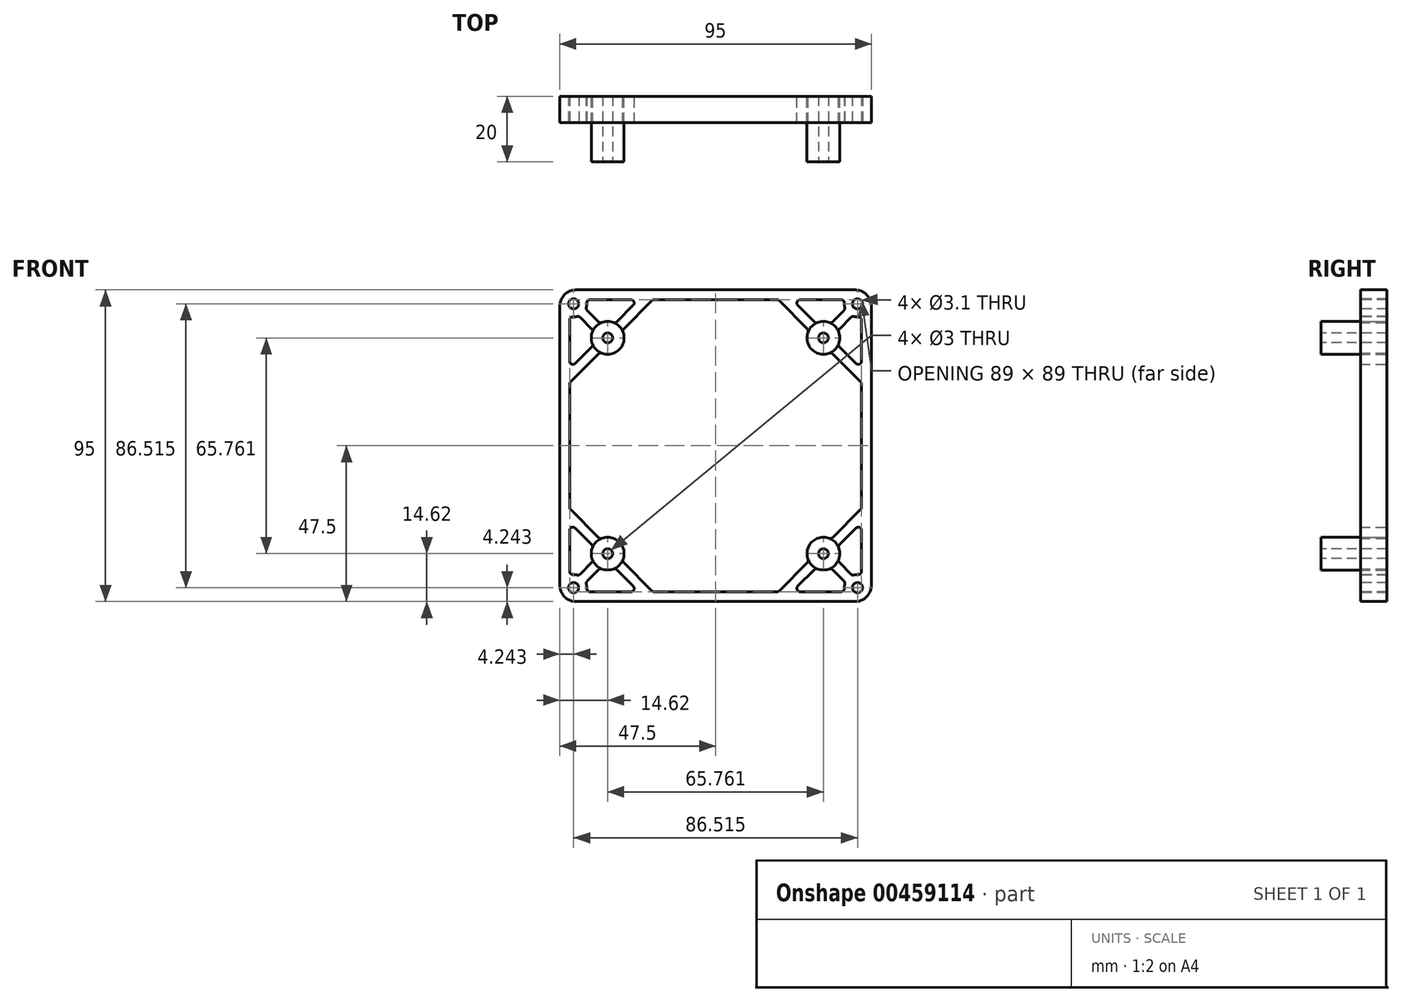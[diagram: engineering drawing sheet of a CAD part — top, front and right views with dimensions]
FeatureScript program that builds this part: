
annotation { "Feature Type Name" : "Feature", "Feature Type Description" : "" }
export const myFeature = defineFeature(function(context is Context, id is Id, definition is map)
    precondition{}
    {
        {
            var Q0;
            Q0=qCreatedBy(makeId("Front.planeOp"),FACE);
            var sketch = newSketch(context, id + "F0", { "sketchPlane" : qUnion([Q0])});
            skCircle(sketch, "E0", {"center": v(0, 0) * mm, "radius": 46.5 * mm, "construction": true});
            skLineSegment(sketch, "E1.bottom", {"start": v(-47.5, 47.5) * mm, "end": v(47.5, 47.5) * mm});
            skLineSegment(sketch, "E1.top", {"start": v(-47.5, -47.5) * mm, "end": v(47.5, -47.5) * mm});
            skLineSegment(sketch, "E1.left", {"start": v(-47.5, 47.5) * mm, "end": v(-47.5, -47.5) * mm});
            skLineSegment(sketch, "E1.right", {"start": v(47.5, 47.5) * mm, "end": v(47.5, -47.5) * mm});
            skLineSegment(sketch, "E2", {"start": v(-47.5, 47.5) * mm, "end": v(0, 0) * mm, "construction": true});
            skLineSegment(sketch, "E3", {"start": v(0, 0) * mm, "end": v(-47.5, 0) * mm, "construction": true});
            skSolve(sketch);
        }
        {
            var Q0;
            Q0=qSketchRegion(id+"F0",true);
            extrude(context, id + "F1", {"entities" : qUnion([Q0]), "depth" : 8 * mm});
        }
        {
            var Q0;
            Q0=makeQuery(id+"F1.opExtrude","CAP_FACE",FACE,{"disambiguationData":[OSD([sQuery(id+"F0.wireOp",EDGE,"E1.bottom"),sQuery(id+"F0.wireOp",EDGE,"E1.top"),sQuery(id+"F0.wireOp",EDGE,"E1.left"),sQuery(id+"F0.wireOp",EDGE,"E1.right"),sQuery(id+"F0.wireOp",EDGE,"Br8Wk0Kl-JEZb-qdU3-erjV-k9UwIw1fq8sk"),sQuery(id+"F0.wireOp",EDGE,"a4S6U98I-Ht7V-EsoT-nMCl-3wyK6It4gxP9"),sQuery(id+"F0.wireOp",EDGE,"JVSH8V9o-5ynY-7XZ7-INyu-qKdjU10l5uuq"),sQuery(id+"F0.wireOp",EDGE,"e923e9d5-6f60-4271-b24b-f0056a6a55640.MirrorCS"),sQuery(id+"F0.wireOp",EDGE,"e923e9d5-6f60-4271-b24b-f0056a6a55641.MirrorCS"),sQuery(id+"F0.wireOp",EDGE,"6366cbee-bac9-4992-bea0-77eb415f6a07.1.0"),sQuery(id+"F0.wireOp",EDGE,"6366cbee-bac9-4992-bea0-77eb415f6a07.1.1"),sQuery(id+"F0.wireOp",EDGE,"6366cbee-bac9-4992-bea0-77eb415f6a07.1.2"),sQuery(id+"F0.wireOp",EDGE,"6366cbee-bac9-4992-bea0-77eb415f6a07.1.3"),sQuery(id+"F0.wireOp",EDGE,"6366cbee-bac9-4992-bea0-77eb415f6a07.1.4"),sQuery(id+"F0.wireOp",EDGE,"6366cbee-bac9-4992-bea0-77eb415f6a07.2.0"),sQuery(id+"F0.wireOp",EDGE,"6366cbee-bac9-4992-bea0-77eb415f6a07.2.1"),sQuery(id+"F0.wireOp",EDGE,"6366cbee-bac9-4992-bea0-77eb415f6a07.2.2"),sQuery(id+"F0.wireOp",EDGE,"6366cbee-bac9-4992-bea0-77eb415f6a07.2.3"),sQuery(id+"F0.wireOp",EDGE,"6366cbee-bac9-4992-bea0-77eb415f6a07.2.4"),sQuery(id+"F0.wireOp",EDGE,"6366cbee-bac9-4992-bea0-77eb415f6a07.3.0"),sQuery(id+"F0.wireOp",EDGE,"6366cbee-bac9-4992-bea0-77eb415f6a07.3.1"),sQuery(id+"F0.wireOp",EDGE,"6366cbee-bac9-4992-bea0-77eb415f6a07.3.2"),sQuery(id+"F0.wireOp",EDGE,"6366cbee-bac9-4992-bea0-77eb415f6a07.3.3"),sQuery(id+"F0.wireOp",EDGE,"6366cbee-bac9-4992-bea0-77eb415f6a07.3.4")])],"isStart":false});
            var sketch = newSketch(context, id + "F2", { "sketchPlane" : qUnion([Q0])});
            skCircle(sketch, "E4", {"center": v(-43.26, 43.26) * mm, "radius": 1.55 * mm});
            skLineSegment(sketch, "E5", {"start": v(-34.04, 47.5) * mm, "end": v(-47.5, 47.5) * mm, "construction": true});
            skLineSegment(sketch, "E6", {"start": v(-47.5, 43.51) * mm, "end": v(-47.5, 47.5) * mm});
            skLineSegment(sketch, "E7", {"start": v(-47.5, 47.5) * mm, "end": v(0, 0) * mm, "construction": true});
            skCircle(sketch, "E8.1.0", {"center": v(-43.26, -43.26) * mm, "radius": 1.55 * mm});
            skCircle(sketch, "E8.2.0", {"center": v(43.26, -43.26) * mm, "radius": 1.55 * mm});
            skCircle(sketch, "E8.3.0", {"center": v(43.26, 43.26) * mm, "radius": 1.55 * mm});
            skPoint(sketch, "E8.center", {"position": v(0, 0) * mm});
            skSolve(sketch);
        }
        {
            var Q0;
            Q0=qSketchRegion(id+"F2",true);
            extrude(context, id + "F3", {"entities" : qUnion([Q0]), "operationType" : NewBodyOperationType.REMOVE, "endBound" : BoundingType.THROUGH_ALL, "oppositeDirection" : true, "depth" : 25 * mm, "offsetDistance" : 25 * mm});
        }
        {
            var Q0;
            Q0=makeQuery(id+"F1.opExtrude","CAP_FACE",FACE,{"disambiguationData":[OSD([sQuery(id+"F0.wireOp",EDGE,"E1.bottom"),sQuery(id+"F0.wireOp",EDGE,"E1.top"),sQuery(id+"F0.wireOp",EDGE,"E1.left"),sQuery(id+"F0.wireOp",EDGE,"E1.right")])],"isStart":false});
            var sketch = newSketch(context, id + "F4", { "sketchPlane" : qUnion([Q0])});
            skLineSegment(sketch, "E9", {"start": v(0, 0) * mm, "end": v(-46.04, 46.04) * mm, "construction": true});
            skLineSegment(sketch, "E10", {"start": v(-32.88, 32.88) * mm, "end": v(-47.5, 18.26) * mm, "construction": true});
            skLineSegment(sketch, "E11", {"start": v(0, 0) * mm, "end": v(-47.5, 0) * mm, "construction": true});
            skLineSegment(sketch, "E12", {"start": v(-44.5, 0) * mm, "end": v(-44.5, 19.14) * mm});
            skLineSegment(sketch, "E13", {"start": v(-44.5, 19.14) * mm, "end": v(-31.82, 31.82) * mm});
            skLineSegment(sketch, "E14", {"start": v(-35, 32.88) * mm, "end": v(-44.5, 23.38) * mm});
            skLineSegment(sketch, "E15", {"start": v(-44.5, 23.38) * mm, "end": v(-44.5, 39.46) * mm});
            skLineSegment(sketch, "E16", {"start": v(-41.7, 39.57) * mm, "end": v(-35, 32.88) * mm});
            skArc(sketch, "E17", {"start": v(-44.5, 39.46) * mm, "mid": v(-42.33, 39.37) * mm, "end": v(-40.43, 40.43) * mm});
            skArc(sketch, "E18.MirrorCS", {"start": v(-39.46, 44.5) * mm, "mid": v(-39.37, 42.33) * mm, "end": v(-40.43, 40.43) * mm});
            skLineSegment(sketch, "E19.MirrorCS", {"start": v(0, 44.5) * mm, "end": v(-19.14, 44.5) * mm});
            skLineSegment(sketch, "E20.MirrorCS", {"start": v(-32.88, 35) * mm, "end": v(-23.38, 44.5) * mm});
            skLineSegment(sketch, "E21.MirrorCS", {"start": v(-32.88, 32.88) * mm, "end": v(-18.26, 47.5) * mm, "construction": true});
            skLineSegment(sketch, "E22.MirrorCS", {"start": v(-23.38, 44.5) * mm, "end": v(-39.46, 44.5) * mm});
            skLineSegment(sketch, "E23.MirrorCS", {"start": v(-39.57, 41.7) * mm, "end": v(-32.88, 35) * mm});
            skLineSegment(sketch, "E24.MirrorCS", {"start": v(-19.14, 44.5) * mm, "end": v(-31.82, 31.82) * mm});
            skLineSegment(sketch, "E25.1.0", {"start": v(-19.14, -44.5) * mm, "end": v(-31.82, -31.82) * mm});
            skLineSegment(sketch, "E25.1.1", {"start": v(-44.5, 0) * mm, "end": v(-44.5, -19.14) * mm});
            skLineSegment(sketch, "E25.1.2", {"start": v(-39.57, -41.7) * mm, "end": v(-32.88, -35) * mm});
            skLineSegment(sketch, "E25.1.3", {"start": v(-32.88, -35) * mm, "end": v(-23.38, -44.5) * mm});
            skLineSegment(sketch, "E25.1.4", {"start": v(-44.5, -23.38) * mm, "end": v(-44.5, -39.46) * mm});
            skLineSegment(sketch, "E25.1.5", {"start": v(0, -44.5) * mm, "end": v(-19.14, -44.5) * mm});
            skLineSegment(sketch, "E25.1.6", {"start": v(-23.38, -44.5) * mm, "end": v(-39.46, -44.5) * mm});
            skLineSegment(sketch, "E25.1.7", {"start": v(-41.7, -39.57) * mm, "end": v(-35, -32.88) * mm});
            skLineSegment(sketch, "E25.1.8", {"start": v(-44.5, -19.14) * mm, "end": v(-31.82, -31.82) * mm});
            skLineSegment(sketch, "E25.1.9", {"start": v(-35, -32.88) * mm, "end": v(-44.5, -23.38) * mm});
            skArc(sketch, "E25.1.10", {"start": v(-44.5, -39.46) * mm, "mid": v(-42.33, -39.37) * mm, "end": v(-40.43, -40.43) * mm});
            skArc(sketch, "E25.1.11", {"start": v(-39.46, -44.5) * mm, "mid": v(-39.37, -42.33) * mm, "end": v(-40.43, -40.43) * mm});
            skLineSegment(sketch, "E25.2.0", {"start": v(44.5, -19.14) * mm, "end": v(31.82, -31.82) * mm});
            skLineSegment(sketch, "E25.2.1", {"start": v(0, -44.5) * mm, "end": v(19.14, -44.5) * mm});
            skLineSegment(sketch, "E25.2.2", {"start": v(41.7, -39.57) * mm, "end": v(35, -32.88) * mm});
            skLineSegment(sketch, "E25.2.3", {"start": v(35, -32.88) * mm, "end": v(44.5, -23.38) * mm});
            skLineSegment(sketch, "E25.2.4", {"start": v(23.38, -44.5) * mm, "end": v(39.46, -44.5) * mm});
            skLineSegment(sketch, "E25.2.5", {"start": v(44.5, 0) * mm, "end": v(44.5, -19.14) * mm});
            skLineSegment(sketch, "E25.2.6", {"start": v(44.5, -23.38) * mm, "end": v(44.5, -39.46) * mm});
            skLineSegment(sketch, "E25.2.7", {"start": v(39.57, -41.7) * mm, "end": v(32.88, -35) * mm});
            skLineSegment(sketch, "E25.2.8", {"start": v(19.14, -44.5) * mm, "end": v(31.82, -31.82) * mm});
            skLineSegment(sketch, "E25.2.9", {"start": v(32.88, -35) * mm, "end": v(23.38, -44.5) * mm});
            skArc(sketch, "E25.2.10", {"start": v(39.46, -44.5) * mm, "mid": v(39.37, -42.33) * mm, "end": v(40.43, -40.43) * mm});
            skArc(sketch, "E25.2.11", {"start": v(44.5, -39.46) * mm, "mid": v(42.33, -39.37) * mm, "end": v(40.43, -40.43) * mm});
            skLineSegment(sketch, "E25.3.0", {"start": v(19.14, 44.5) * mm, "end": v(31.82, 31.82) * mm});
            skLineSegment(sketch, "E25.3.1", {"start": v(44.5, 0) * mm, "end": v(44.5, 19.14) * mm});
            skLineSegment(sketch, "E25.3.2", {"start": v(39.57, 41.7) * mm, "end": v(32.88, 35) * mm});
            skLineSegment(sketch, "E25.3.3", {"start": v(32.88, 35) * mm, "end": v(23.38, 44.5) * mm});
            skLineSegment(sketch, "E25.3.4", {"start": v(44.5, 23.38) * mm, "end": v(44.5, 39.46) * mm});
            skLineSegment(sketch, "E25.3.5", {"start": v(0, 44.5) * mm, "end": v(19.14, 44.5) * mm});
            skLineSegment(sketch, "E25.3.6", {"start": v(23.38, 44.5) * mm, "end": v(39.46, 44.5) * mm});
            skLineSegment(sketch, "E25.3.7", {"start": v(41.7, 39.57) * mm, "end": v(35, 32.88) * mm});
            skLineSegment(sketch, "E25.3.8", {"start": v(44.5, 19.14) * mm, "end": v(31.82, 31.82) * mm});
            skLineSegment(sketch, "E25.3.9", {"start": v(35, 32.88) * mm, "end": v(44.5, 23.38) * mm});
            skArc(sketch, "E25.3.10", {"start": v(44.5, 39.46) * mm, "mid": v(42.33, 39.37) * mm, "end": v(40.43, 40.43) * mm});
            skArc(sketch, "E25.3.11", {"start": v(39.46, 44.5) * mm, "mid": v(39.37, 42.33) * mm, "end": v(40.43, 40.43) * mm});
            skPoint(sketch, "E25.center", {"position": v(0, 0) * mm});
            skSolve(sketch);
        }
        {
            var Q0;
            Q0 = qSketchRegion(id + "F4", true);
            extrude(context, id + "F5", {"entities" : qUnion([Q0]), "operationType" : NewBodyOperationType.REMOVE, "endBound" : BoundingType.THROUGH_ALL, "oppositeDirection" : true, "depth" : 25 * mm, "offsetDistance" : 25 * mm});
        }
        {
            var Q0;
            Q0=makeQuery(id+"F1.opExtrude","CAP_FACE",FACE,{"disambiguationData":[OSD([sQuery(id+"F0.wireOp",EDGE,"E1.bottom"),sQuery(id+"F0.wireOp",EDGE,"E1.top"),sQuery(id+"F0.wireOp",EDGE,"E1.left"),sQuery(id+"F0.wireOp",EDGE,"E1.right")])],"isStart":true});
            var sketch = newSketch(context, id + "F6", { "sketchPlane" : qUnion([Q0])});
            skCircle(sketch, "E26", {"center": v(-32.88, 32.88) * mm, "radius": 5 * mm});
            skCircle(sketch, "E27.1.0", {"center": v(-32.88, -32.88) * mm, "radius": 5 * mm});
            skCircle(sketch, "E27.2.0", {"center": v(32.88, -32.88) * mm, "radius": 5 * mm});
            skCircle(sketch, "E27.3.0", {"center": v(32.88, 32.88) * mm, "radius": 5 * mm});
            skPoint(sketch, "E27.center", {"position": v(0, 0) * mm});
            skSolve(sketch);
        }
        {
            var Q0;
            Q0=qSketchRegion(id+"F6",true);
            extrude(context, id + "F7", {"entities" : qUnion([Q0]), "operationType" : NewBodyOperationType.ADD, "oppositeDirection" : true, "depth" : 20 * mm, "offsetDistance" : 25 * mm});
        }
        {
            var Q0;
            Q0=makeQuery(id+"F7.opExtrude","CAP_FACE",FACE,{"disambiguationData":[OSD([sQuery(id+"F6.wireOp",EDGE,"E27.2.0")])],"isStart":false});
            var sketch = newSketch(context, id + "F8", { "sketchPlane" : qUnion([Q0])});
            skCircle(sketch, "E28", {"center": v(-32.88, -32.88) * mm, "radius": 1.5 * mm});
            skCircle(sketch, "E29.1.0", {"center": v(32.88, -32.88) * mm, "radius": 1.5 * mm});
            skCircle(sketch, "E29.2.0", {"center": v(32.88, 32.88) * mm, "radius": 1.5 * mm});
            skCircle(sketch, "E29.3.0", {"center": v(-32.88, 32.88) * mm, "radius": 1.5 * mm});
            skPoint(sketch, "E29.center", {"position": v(0, 0) * mm});
            skSolve(sketch);
        }
        {
            var Q0;
            Q0=qSketchRegion(id+"F8",true);
            extrude(context, id + "F9", {"entities" : qUnion([Q0]), "operationType" : NewBodyOperationType.REMOVE, "endBound" : BoundingType.THROUGH_ALL, "oppositeDirection" : true, "depth" : 25 * mm});
        }
        {
            var Q0;
            Q0=makeQuery(id+"F1.opExtrude","CAP_FACE",FACE,{"disambiguationData":[OSD([sQuery(id+"F0.wireOp",EDGE,"E1.bottom"),sQuery(id+"F0.wireOp",EDGE,"E1.top"),sQuery(id+"F0.wireOp",EDGE,"E1.left"),sQuery(id+"F0.wireOp",EDGE,"E1.right"),sQuery(id+"F0.wireOp",EDGE,"Br8Wk0Kl-JEZb-qdU3-erjV-k9UwIw1fq8sk"),sQuery(id+"F0.wireOp",EDGE,"a4S6U98I-Ht7V-EsoT-nMCl-3wyK6It4gxP9"),sQuery(id+"F0.wireOp",EDGE,"JVSH8V9o-5ynY-7XZ7-INyu-qKdjU10l5uuq"),sQuery(id+"F0.wireOp",EDGE,"e923e9d5-6f60-4271-b24b-f0056a6a55640.MirrorCS"),sQuery(id+"F0.wireOp",EDGE,"e923e9d5-6f60-4271-b24b-f0056a6a55641.MirrorCS"),sQuery(id+"F0.wireOp",EDGE,"6366cbee-bac9-4992-bea0-77eb415f6a07.1.0"),sQuery(id+"F0.wireOp",EDGE,"6366cbee-bac9-4992-bea0-77eb415f6a07.1.1"),sQuery(id+"F0.wireOp",EDGE,"6366cbee-bac9-4992-bea0-77eb415f6a07.1.2"),sQuery(id+"F0.wireOp",EDGE,"6366cbee-bac9-4992-bea0-77eb415f6a07.1.3"),sQuery(id+"F0.wireOp",EDGE,"6366cbee-bac9-4992-bea0-77eb415f6a07.1.4"),sQuery(id+"F0.wireOp",EDGE,"6366cbee-bac9-4992-bea0-77eb415f6a07.2.0"),sQuery(id+"F0.wireOp",EDGE,"6366cbee-bac9-4992-bea0-77eb415f6a07.2.1"),sQuery(id+"F0.wireOp",EDGE,"6366cbee-bac9-4992-bea0-77eb415f6a07.2.2"),sQuery(id+"F0.wireOp",EDGE,"6366cbee-bac9-4992-bea0-77eb415f6a07.2.3"),sQuery(id+"F0.wireOp",EDGE,"6366cbee-bac9-4992-bea0-77eb415f6a07.2.4"),sQuery(id+"F0.wireOp",EDGE,"6366cbee-bac9-4992-bea0-77eb415f6a07.3.0"),sQuery(id+"F0.wireOp",EDGE,"6366cbee-bac9-4992-bea0-77eb415f6a07.3.1"),sQuery(id+"F0.wireOp",EDGE,"6366cbee-bac9-4992-bea0-77eb415f6a07.3.2"),sQuery(id+"F0.wireOp",EDGE,"6366cbee-bac9-4992-bea0-77eb415f6a07.3.3"),sQuery(id+"F0.wireOp",EDGE,"6366cbee-bac9-4992-bea0-77eb415f6a07.3.4")])],"isStart":true});
            var sketch = newSketch(context, id + "F10", { "sketchPlane" : qUnion([Q0])});
            skLineSegment(sketch, "E30", {"start": v(-32.88, 27.88) * mm, "end": v(-32.88, -32.88) * mm, "construction": true});
            skLineSegment(sketch, "E31", {"start": v(-32.88, -32.88) * mm, "end": v(-27.88, -32.88) * mm, "construction": true});
            skLineSegment(sketch, "E32", {"start": v(-32.88, -36.92) * mm, "end": v(-29.38, -34.9) * mm});
            skLineSegment(sketch, "E33", {"start": v(-29.38, -34.9) * mm, "end": v(-29.38, -32.88) * mm});
            skLineSegment(sketch, "E34.MirrorCS", {"start": v(-29.38, -30.86) * mm, "end": v(-29.38, -32.88) * mm});
            skLineSegment(sketch, "E35.MirrorCS", {"start": v(-32.88, -28.84) * mm, "end": v(-29.38, -30.86) * mm});
            skLineSegment(sketch, "E36.MirrorCS", {"start": v(-32.88, -36.92) * mm, "end": v(-36.38, -34.9) * mm});
            skLineSegment(sketch, "E37.MirrorCS", {"start": v(-36.38, -34.9) * mm, "end": v(-36.38, -32.88) * mm});
            skLineSegment(sketch, "E38.MirrorCS", {"start": v(-32.88, -28.84) * mm, "end": v(-36.38, -30.86) * mm});
            skLineSegment(sketch, "E39.MirrorCS", {"start": v(-36.38, -30.86) * mm, "end": v(-36.38, -32.88) * mm});
            skLineSegment(sketch, "E40", {"start": v(0, 47.5) * mm, "end": v(0, 0) * mm, "construction": true});
            skLineSegment(sketch, "E41", {"start": v(0, 0) * mm, "end": v(-47.5, 0) * mm, "construction": true});
            skLineSegment(sketch, "E42.MirrorCS", {"start": v(29.38, -30.86) * mm, "end": v(29.38, -32.88) * mm});
            skLineSegment(sketch, "E43.MirrorCS", {"start": v(36.38, -30.86) * mm, "end": v(36.38, -32.88) * mm});
            skLineSegment(sketch, "E44.MirrorCS", {"start": v(32.88, -36.92) * mm, "end": v(29.38, -34.9) * mm});
            skLineSegment(sketch, "E45.MirrorCS", {"start": v(36.38, -34.9) * mm, "end": v(36.38, -32.88) * mm});
            skLineSegment(sketch, "E46.MirrorCS", {"start": v(29.38, -34.9) * mm, "end": v(29.38, -32.88) * mm});
            skLineSegment(sketch, "E47.MirrorCS", {"start": v(32.88, -36.92) * mm, "end": v(36.38, -34.9) * mm});
            skLineSegment(sketch, "E48.MirrorCS", {"start": v(32.88, -32.88) * mm, "end": v(27.88, -32.88) * mm, "construction": true});
            skLineSegment(sketch, "E49.MirrorCS", {"start": v(32.88, 27.88) * mm, "end": v(32.88, -32.88) * mm, "construction": true});
            skLineSegment(sketch, "E50.MirrorCS", {"start": v(32.88, -28.84) * mm, "end": v(29.38, -30.86) * mm});
            skLineSegment(sketch, "E51.MirrorCS", {"start": v(32.88, -28.84) * mm, "end": v(36.38, -30.86) * mm});
            skLineSegment(sketch, "E52.MirrorCS", {"start": v(-32.88, 36.92) * mm, "end": v(-29.38, 34.9) * mm});
            skLineSegment(sketch, "E53.MirrorCS", {"start": v(-29.38, 34.9) * mm, "end": v(-29.38, 32.88) * mm});
            skLineSegment(sketch, "E54.MirrorCS", {"start": v(32.88, 36.92) * mm, "end": v(29.38, 34.9) * mm});
            skLineSegment(sketch, "E55.MirrorCS", {"start": v(-36.38, 34.9) * mm, "end": v(-36.38, 32.88) * mm});
            skLineSegment(sketch, "E56.MirrorCS", {"start": v(36.38, 30.86) * mm, "end": v(36.38, 32.88) * mm});
            skLineSegment(sketch, "E57.MirrorCS", {"start": v(29.38, 30.86) * mm, "end": v(29.38, 32.88) * mm});
            skLineSegment(sketch, "E58.MirrorCS", {"start": v(29.38, 34.9) * mm, "end": v(29.38, 32.88) * mm});
            skLineSegment(sketch, "E59.MirrorCS", {"start": v(-36.38, 30.86) * mm, "end": v(-36.38, 32.88) * mm});
            skLineSegment(sketch, "E60.MirrorCS", {"start": v(-29.38, 30.86) * mm, "end": v(-29.38, 32.88) * mm});
            skLineSegment(sketch, "E61.MirrorCS", {"start": v(36.38, 34.9) * mm, "end": v(36.38, 32.88) * mm});
            skLineSegment(sketch, "E62.MirrorCS", {"start": v(-32.88, 36.92) * mm, "end": v(-36.38, 34.9) * mm});
            skLineSegment(sketch, "E63.MirrorCS", {"start": v(-32.88, -27.88) * mm, "end": v(-32.88, 32.88) * mm, "construction": true});
            skLineSegment(sketch, "E64.MirrorCS", {"start": v(-32.88, 28.84) * mm, "end": v(-29.38, 30.86) * mm});
            skLineSegment(sketch, "E65.MirrorCS", {"start": v(-32.88, 28.84) * mm, "end": v(-36.38, 30.86) * mm});
            skLineSegment(sketch, "E66.MirrorCS", {"start": v(32.88, 28.84) * mm, "end": v(29.38, 30.86) * mm});
            skLineSegment(sketch, "E67.MirrorCS", {"start": v(32.88, 32.88) * mm, "end": v(27.88, 32.88) * mm, "construction": true});
            skLineSegment(sketch, "E68.MirrorCS", {"start": v(32.88, 36.92) * mm, "end": v(36.38, 34.9) * mm});
            skLineSegment(sketch, "E69.MirrorCS", {"start": v(32.88, 28.84) * mm, "end": v(36.38, 30.86) * mm});
            skLineSegment(sketch, "E70.MirrorCS", {"start": v(-32.88, 32.88) * mm, "end": v(-27.88, 32.88) * mm, "construction": true});
            skLineSegment(sketch, "E71.MirrorCS", {"start": v(32.88, -27.88) * mm, "end": v(32.88, 32.88) * mm, "construction": true});
            skSolve(sketch);
        }
        {
            var Q0;
            Q0=makeQuery(id+"F1.opExtrude","SWEPT_EDGE",EDGE,{"disambiguationData":[OSD([sQuery(id+"F0.wireOp",EDGE,"E1.bottom"),sQuery(id+"F0.wireOp",EDGE,"E1.left")])]});
            var Q1;
            Q1=makeQuery(id+"F1.opExtrude","SWEPT_EDGE",EDGE,{"disambiguationData":[OSD([sQuery(id+"F0.wireOp",EDGE,"E1.bottom"),sQuery(id+"F0.wireOp",EDGE,"E1.right")])]});
            var Q2;
            Q2=makeQuery(id+"F1.opExtrude","SWEPT_EDGE",EDGE,{"disambiguationData":[OSD([sQuery(id+"F0.wireOp",EDGE,"E1.top"),sQuery(id+"F0.wireOp",EDGE,"E1.right")])]});
            var Q3;
            Q3=makeQuery(id+"F1.opExtrude","SWEPT_EDGE",EDGE,{"disambiguationData":[OSD([sQuery(id+"F0.wireOp",EDGE,"E1.top"),sQuery(id+"F0.wireOp",EDGE,"E1.left")])]});
            fillet(context, id + "F11", {"entities" : qUnion([Q0, Q1, Q2, Q3]), "radius" : 5 * mm, "tangentPropagation" : true, "allowEdgeOverflow" : false});
        }
        {
            var Q0;
            Q0=makeQuery(id+"F5.boolean.opBoolean","COPY",EDGE,{"derivedFrom":makeQuery(id+"F5.opExtrude","SWEPT_EDGE",EDGE,{"disambiguationData":[OSD([sQuery(id+"F4.wireOp",EDGE,"E18.MirrorCS"),sQuery(id+"F4.wireOp",EDGE,"E22.MirrorCS")])]})});
            var Q1;
            Q1=makeQuery(id+"F5.boolean.opBoolean","COPY",EDGE,{"derivedFrom":makeQuery(id+"F5.opExtrude","SWEPT_EDGE",EDGE,{"disambiguationData":[OSD([sQuery(id+"F4.wireOp",EDGE,"E18.MirrorCS"),sQuery(id+"F4.wireOp",EDGE,"E23.MirrorCS")])]})});
            var Q2;
            Q2=makeQuery(id+"F5.boolean.opBoolean","COPY",EDGE,{"derivedFrom":makeQuery(id+"F5.opExtrude","SWEPT_EDGE",EDGE,{"disambiguationData":[OSD([sQuery(id+"F4.wireOp",EDGE,"E20.MirrorCS"),sQuery(id+"F4.wireOp",EDGE,"E22.MirrorCS")])]})});
            var Q3;
            Q3=makeQuery(id+"F7.boolean.opBoolean","INTERSECT",EDGE,{"derivedFrom":[makeQuery(id+"F5.boolean.opBoolean","COPY",FACE,{"derivedFrom":makeQuery(id+"F5.opExtrude","SWEPT_FACE",FACE,{"disambiguationData":[OSD([sQuery(id+"F4.wireOp",EDGE,"E20.MirrorCS")])]})}),makeQuery(id+"F7.opExtrude","SWEPT_FACE",FACE,{"disambiguationData":[OSD([sQuery(id+"F6.wireOp",EDGE,"E27.3.0")])]})]});
            var Q4;
            Q4=makeQuery(id+"F7.boolean.opBoolean","INTERSECT",EDGE,{"derivedFrom":[makeQuery(id+"F5.boolean.opBoolean","COPY",FACE,{"derivedFrom":makeQuery(id+"F5.opExtrude","SWEPT_FACE",FACE,{"disambiguationData":[OSD([sQuery(id+"F4.wireOp",EDGE,"E23.MirrorCS")])]})}),makeQuery(id+"F7.opExtrude","SWEPT_FACE",FACE,{"disambiguationData":[OSD([sQuery(id+"F6.wireOp",EDGE,"E27.3.0")])]})]});
            var Q5;
            Q5=makeQuery(id+"F7.boolean.opBoolean","INTERSECT",EDGE,{"derivedFrom":[makeQuery(id+"F5.boolean.opBoolean","COPY",FACE,{"derivedFrom":makeQuery(id+"F5.opExtrude","SWEPT_FACE",FACE,{"disambiguationData":[OSD([sQuery(id+"F4.wireOp",EDGE,"E16")])]})}),makeQuery(id+"F7.opExtrude","SWEPT_FACE",FACE,{"disambiguationData":[OSD([sQuery(id+"F6.wireOp",EDGE,"E27.3.0")])]})]});
            var Q6;
            Q6=makeQuery(id+"F7.boolean.opBoolean","INTERSECT",EDGE,{"derivedFrom":[makeQuery(id+"F5.boolean.opBoolean","COPY",FACE,{"derivedFrom":makeQuery(id+"F5.opExtrude","SWEPT_FACE",FACE,{"disambiguationData":[OSD([sQuery(id+"F4.wireOp",EDGE,"E14")])]})}),makeQuery(id+"F7.opExtrude","SWEPT_FACE",FACE,{"disambiguationData":[OSD([sQuery(id+"F6.wireOp",EDGE,"E27.3.0")])]})]});
            var Q7;
            Q7=makeQuery(id+"F5.boolean.opBoolean","COPY",EDGE,{"derivedFrom":makeQuery(id+"F5.opExtrude","SWEPT_EDGE",EDGE,{"disambiguationData":[OSD([sQuery(id+"F4.wireOp",EDGE,"E14"),sQuery(id+"F4.wireOp",EDGE,"E15")])]})});
            var Q8;
            Q8=makeQuery(id+"F5.boolean.opBoolean","COPY",EDGE,{"derivedFrom":makeQuery(id+"F5.opExtrude","SWEPT_EDGE",EDGE,{"disambiguationData":[OSD([sQuery(id+"F4.wireOp",EDGE,"E16"),sQuery(id+"F4.wireOp",EDGE,"E17")])]})});
            var Q9;
            Q9=makeQuery(id+"F5.boolean.opBoolean","COPY",EDGE,{"derivedFrom":makeQuery(id+"F5.opExtrude","SWEPT_EDGE",EDGE,{"disambiguationData":[OSD([sQuery(id+"F4.wireOp",EDGE,"E15"),sQuery(id+"F4.wireOp",EDGE,"E17")])]})});
            var Q10;
            Q10=makeQuery(id+"F5.boolean.opBoolean","COPY",EDGE,{"derivedFrom":makeQuery(id+"F5.opExtrude","SWEPT_EDGE",EDGE,{"disambiguationData":[OSD([sQuery(id+"F4.wireOp",EDGE,"E12"),sQuery(id+"F4.wireOp",EDGE,"E13")])]})});
            var Q11;
            Q11=makeQuery(id+"F5.boolean.opBoolean","COPY",EDGE,{"derivedFrom":makeQuery(id+"F5.opExtrude","SWEPT_EDGE",EDGE,{"disambiguationData":[OSD([sQuery(id+"F4.wireOp",EDGE,"E19.MirrorCS"),sQuery(id+"F4.wireOp",EDGE,"E24.MirrorCS")])]})});
            var Q12;
            Q12=makeQuery(id+"F7.boolean.opBoolean","INTERSECT",EDGE,{"disambiguationData":[OD(0.0)],"derivedFrom":[makeQuery(id+"F5.boolean.opBoolean","COPY",FACE,{"derivedFrom":makeQuery(id+"F5.opExtrude","SWEPT_FACE",FACE,{"disambiguationData":[OSD([sQuery(id+"F4.wireOp",EDGE,"E13"),sQuery(id+"F4.wireOp",EDGE,"E24.MirrorCS")])]})}),makeQuery(id+"F7.opExtrude","SWEPT_FACE",FACE,{"disambiguationData":[OSD([sQuery(id+"F6.wireOp",EDGE,"E27.3.0")])]})]});
            var Q13;
            Q13=makeQuery(id+"F7.boolean.opBoolean","INTERSECT",EDGE,{"disambiguationData":[OD(1.0)],"derivedFrom":[makeQuery(id+"F5.boolean.opBoolean","COPY",FACE,{"derivedFrom":makeQuery(id+"F5.opExtrude","SWEPT_FACE",FACE,{"disambiguationData":[OSD([sQuery(id+"F4.wireOp",EDGE,"E13"),sQuery(id+"F4.wireOp",EDGE,"E24.MirrorCS")])]})}),makeQuery(id+"F7.opExtrude","SWEPT_FACE",FACE,{"disambiguationData":[OSD([sQuery(id+"F6.wireOp",EDGE,"E27.3.0")])]})]});
            var Q14;
            Q14=makeQuery(id+"F7.boolean.opBoolean","INTERSECT",EDGE,{"derivedFrom":[makeQuery(id+"F5.boolean.opBoolean","COPY",FACE,{"derivedFrom":makeQuery(id+"F5.opExtrude","SWEPT_FACE",FACE,{"disambiguationData":[OSD([sQuery(id+"F4.wireOp",EDGE,"E25.3.3")])]})}),makeQuery(id+"F7.opExtrude","SWEPT_FACE",FACE,{"disambiguationData":[OSD([sQuery(id+"F6.wireOp",EDGE,"E26")])]})]});
            var Q15;
            Q15=makeQuery(id+"F7.boolean.opBoolean","INTERSECT",EDGE,{"derivedFrom":[makeQuery(id+"F5.boolean.opBoolean","COPY",FACE,{"derivedFrom":makeQuery(id+"F5.opExtrude","SWEPT_FACE",FACE,{"disambiguationData":[OSD([sQuery(id+"F4.wireOp",EDGE,"E25.3.2")])]})}),makeQuery(id+"F7.opExtrude","SWEPT_FACE",FACE,{"disambiguationData":[OSD([sQuery(id+"F6.wireOp",EDGE,"E26")])]})]});
            var Q16;
            Q16=makeQuery(id+"F5.boolean.opBoolean","COPY",EDGE,{"derivedFrom":makeQuery(id+"F5.opExtrude","SWEPT_EDGE",EDGE,{"disambiguationData":[OSD([sQuery(id+"F4.wireOp",EDGE,"E25.3.4"),sQuery(id+"F4.wireOp",EDGE,"E25.3.9")])]})});
            var Q17;
            Q17=makeQuery(id+"F5.boolean.opBoolean","COPY",EDGE,{"derivedFrom":makeQuery(id+"F5.opExtrude","SWEPT_EDGE",EDGE,{"disambiguationData":[OSD([sQuery(id+"F4.wireOp",EDGE,"E25.3.0"),sQuery(id+"F4.wireOp",EDGE,"E25.3.5")])]})});
            var Q18;
            Q18=makeQuery(id+"F7.boolean.opBoolean","INTERSECT",EDGE,{"disambiguationData":[OD(1.0)],"derivedFrom":[makeQuery(id+"F5.boolean.opBoolean","COPY",FACE,{"derivedFrom":makeQuery(id+"F5.opExtrude","SWEPT_FACE",FACE,{"disambiguationData":[OSD([sQuery(id+"F4.wireOp",EDGE,"E25.3.0"),sQuery(id+"F4.wireOp",EDGE,"E25.3.8")])]})}),makeQuery(id+"F7.opExtrude","SWEPT_FACE",FACE,{"disambiguationData":[OSD([sQuery(id+"F6.wireOp",EDGE,"E26")])]})]});
            var Q19;
            Q19=makeQuery(id+"F7.boolean.opBoolean","INTERSECT",EDGE,{"disambiguationData":[OD(0.0)],"derivedFrom":[makeQuery(id+"F5.boolean.opBoolean","COPY",FACE,{"derivedFrom":makeQuery(id+"F5.opExtrude","SWEPT_FACE",FACE,{"disambiguationData":[OSD([sQuery(id+"F4.wireOp",EDGE,"E25.3.0"),sQuery(id+"F4.wireOp",EDGE,"E25.3.8")])]})}),makeQuery(id+"F7.opExtrude","SWEPT_FACE",FACE,{"disambiguationData":[OSD([sQuery(id+"F6.wireOp",EDGE,"E26")])]})]});
            var Q20;
            Q20=makeQuery(id+"F5.boolean.opBoolean","COPY",EDGE,{"derivedFrom":makeQuery(id+"F5.opExtrude","SWEPT_EDGE",EDGE,{"disambiguationData":[OSD([sQuery(id+"F4.wireOp",EDGE,"E25.3.1"),sQuery(id+"F4.wireOp",EDGE,"E25.3.8")])]})});
            var Q21;
            Q21=makeQuery(id+"F5.boolean.opBoolean","COPY",EDGE,{"derivedFrom":makeQuery(id+"F5.opExtrude","SWEPT_EDGE",EDGE,{"disambiguationData":[OSD([sQuery(id+"F4.wireOp",EDGE,"E25.3.6"),sQuery(id+"F4.wireOp",EDGE,"E25.3.11")])]})});
            var Q22;
            Q22=makeQuery(id+"F5.boolean.opBoolean","COPY",EDGE,{"derivedFrom":makeQuery(id+"F5.opExtrude","SWEPT_EDGE",EDGE,{"disambiguationData":[OSD([sQuery(id+"F4.wireOp",EDGE,"E25.3.7"),sQuery(id+"F4.wireOp",EDGE,"E25.3.10")])]})});
            var Q23;
            Q23=makeQuery(id+"F5.boolean.opBoolean","COPY",EDGE,{"derivedFrom":makeQuery(id+"F5.opExtrude","SWEPT_EDGE",EDGE,{"disambiguationData":[OSD([sQuery(id+"F4.wireOp",EDGE,"E25.3.4"),sQuery(id+"F4.wireOp",EDGE,"E25.3.10")])]})});
            var Q24;
            Q24=makeQuery(id+"F7.boolean.opBoolean","INTERSECT",EDGE,{"derivedFrom":[makeQuery(id+"F5.boolean.opBoolean","COPY",FACE,{"derivedFrom":makeQuery(id+"F5.opExtrude","SWEPT_FACE",FACE,{"disambiguationData":[OSD([sQuery(id+"F4.wireOp",EDGE,"E25.3.9")])]})}),makeQuery(id+"F7.opExtrude","SWEPT_FACE",FACE,{"disambiguationData":[OSD([sQuery(id+"F6.wireOp",EDGE,"E26")])]})]});
            var Q25;
            Q25=makeQuery(id+"F5.boolean.opBoolean","COPY",EDGE,{"derivedFrom":makeQuery(id+"F5.opExtrude","SWEPT_EDGE",EDGE,{"disambiguationData":[OSD([sQuery(id+"F4.wireOp",EDGE,"E25.3.3"),sQuery(id+"F4.wireOp",EDGE,"E25.3.6")])]})});
            var Q26;
            Q26=makeQuery(id+"F5.boolean.opBoolean","COPY",EDGE,{"derivedFrom":makeQuery(id+"F5.opExtrude","SWEPT_EDGE",EDGE,{"disambiguationData":[OSD([sQuery(id+"F4.wireOp",EDGE,"E25.3.2"),sQuery(id+"F4.wireOp",EDGE,"E25.3.11")])]})});
            var Q27;
            Q27=makeQuery(id+"F7.boolean.opBoolean","INTERSECT",EDGE,{"derivedFrom":[makeQuery(id+"F5.boolean.opBoolean","COPY",FACE,{"derivedFrom":makeQuery(id+"F5.opExtrude","SWEPT_FACE",FACE,{"disambiguationData":[OSD([sQuery(id+"F4.wireOp",EDGE,"E25.3.7")])]})}),makeQuery(id+"F7.opExtrude","SWEPT_FACE",FACE,{"disambiguationData":[OSD([sQuery(id+"F6.wireOp",EDGE,"E26")])]})]});
            var Q28;
            Q28=makeQuery(id+"F5.boolean.opBoolean","COPY",EDGE,{"derivedFrom":makeQuery(id+"F5.opExtrude","SWEPT_EDGE",EDGE,{"disambiguationData":[OSD([sQuery(id+"F4.wireOp",EDGE,"E25.2.0"),sQuery(id+"F4.wireOp",EDGE,"E25.2.5")])]})});
            var Q29;
            Q29=makeQuery(id+"F7.boolean.opBoolean","INTERSECT",EDGE,{"disambiguationData":[OD(0.0)],"derivedFrom":[makeQuery(id+"F5.boolean.opBoolean","COPY",FACE,{"derivedFrom":makeQuery(id+"F5.opExtrude","SWEPT_FACE",FACE,{"disambiguationData":[OSD([sQuery(id+"F4.wireOp",EDGE,"E25.2.0"),sQuery(id+"F4.wireOp",EDGE,"E25.2.8")])]})}),makeQuery(id+"F7.opExtrude","SWEPT_FACE",FACE,{"disambiguationData":[OSD([sQuery(id+"F6.wireOp",EDGE,"E27.1.0")])]})]});
            var Q30;
            Q30=makeQuery(id+"F7.boolean.opBoolean","INTERSECT",EDGE,{"disambiguationData":[OD(1.0)],"derivedFrom":[makeQuery(id+"F5.boolean.opBoolean","COPY",FACE,{"derivedFrom":makeQuery(id+"F5.opExtrude","SWEPT_FACE",FACE,{"disambiguationData":[OSD([sQuery(id+"F4.wireOp",EDGE,"E25.2.0"),sQuery(id+"F4.wireOp",EDGE,"E25.2.8")])]})}),makeQuery(id+"F7.opExtrude","SWEPT_FACE",FACE,{"disambiguationData":[OSD([sQuery(id+"F6.wireOp",EDGE,"E27.1.0")])]})]});
            var Q31;
            Q31=makeQuery(id+"F5.boolean.opBoolean","COPY",EDGE,{"derivedFrom":makeQuery(id+"F5.opExtrude","SWEPT_EDGE",EDGE,{"disambiguationData":[OSD([sQuery(id+"F4.wireOp",EDGE,"E25.2.1"),sQuery(id+"F4.wireOp",EDGE,"E25.2.8")])]})});
            var Q32;
            Q32=makeQuery(id+"F7.boolean.opBoolean","INTERSECT",EDGE,{"derivedFrom":[makeQuery(id+"F5.boolean.opBoolean","COPY",FACE,{"derivedFrom":makeQuery(id+"F5.opExtrude","SWEPT_FACE",FACE,{"disambiguationData":[OSD([sQuery(id+"F4.wireOp",EDGE,"E25.2.3")])]})}),makeQuery(id+"F7.opExtrude","SWEPT_FACE",FACE,{"disambiguationData":[OSD([sQuery(id+"F6.wireOp",EDGE,"E27.1.0")])]})]});
            var Q33;
            Q33=makeQuery(id+"F7.boolean.opBoolean","INTERSECT",EDGE,{"derivedFrom":[makeQuery(id+"F5.boolean.opBoolean","COPY",FACE,{"derivedFrom":makeQuery(id+"F5.opExtrude","SWEPT_FACE",FACE,{"disambiguationData":[OSD([sQuery(id+"F4.wireOp",EDGE,"E25.2.2")])]})}),makeQuery(id+"F7.opExtrude","SWEPT_FACE",FACE,{"disambiguationData":[OSD([sQuery(id+"F6.wireOp",EDGE,"E27.1.0")])]})]});
            var Q34;
            Q34=makeQuery(id+"F5.boolean.opBoolean","COPY",EDGE,{"derivedFrom":makeQuery(id+"F5.opExtrude","SWEPT_EDGE",EDGE,{"disambiguationData":[OSD([sQuery(id+"F4.wireOp",EDGE,"E25.2.3"),sQuery(id+"F4.wireOp",EDGE,"E25.2.6")])]})});
            var Q35;
            Q35=makeQuery(id+"F7.boolean.opBoolean","INTERSECT",EDGE,{"derivedFrom":[makeQuery(id+"F5.boolean.opBoolean","COPY",FACE,{"derivedFrom":makeQuery(id+"F5.opExtrude","SWEPT_FACE",FACE,{"disambiguationData":[OSD([sQuery(id+"F4.wireOp",EDGE,"E25.2.7")])]})}),makeQuery(id+"F7.opExtrude","SWEPT_FACE",FACE,{"disambiguationData":[OSD([sQuery(id+"F6.wireOp",EDGE,"E27.1.0")])]})]});
            var Q36;
            Q36=makeQuery(id+"F7.boolean.opBoolean","INTERSECT",EDGE,{"derivedFrom":[makeQuery(id+"F5.boolean.opBoolean","COPY",FACE,{"derivedFrom":makeQuery(id+"F5.opExtrude","SWEPT_FACE",FACE,{"disambiguationData":[OSD([sQuery(id+"F4.wireOp",EDGE,"E25.2.9")])]})}),makeQuery(id+"F7.opExtrude","SWEPT_FACE",FACE,{"disambiguationData":[OSD([sQuery(id+"F6.wireOp",EDGE,"E27.1.0")])]})]});
            var Q37;
            Q37=makeQuery(id+"F5.boolean.opBoolean","COPY",EDGE,{"derivedFrom":makeQuery(id+"F5.opExtrude","SWEPT_EDGE",EDGE,{"disambiguationData":[OSD([sQuery(id+"F4.wireOp",EDGE,"E25.2.6"),sQuery(id+"F4.wireOp",EDGE,"E25.2.11")])]})});
            var Q38;
            Q38=makeQuery(id+"F5.boolean.opBoolean","COPY",EDGE,{"derivedFrom":makeQuery(id+"F5.opExtrude","SWEPT_EDGE",EDGE,{"disambiguationData":[OSD([sQuery(id+"F4.wireOp",EDGE,"E25.2.2"),sQuery(id+"F4.wireOp",EDGE,"E25.2.11")])]})});
            var Q39;
            Q39=makeQuery(id+"F5.boolean.opBoolean","COPY",EDGE,{"derivedFrom":makeQuery(id+"F5.opExtrude","SWEPT_EDGE",EDGE,{"disambiguationData":[OSD([sQuery(id+"F4.wireOp",EDGE,"E25.2.7"),sQuery(id+"F4.wireOp",EDGE,"E25.2.10")])]})});
            var Q40;
            Q40=makeQuery(id+"F5.boolean.opBoolean","COPY",EDGE,{"derivedFrom":makeQuery(id+"F5.opExtrude","SWEPT_EDGE",EDGE,{"disambiguationData":[OSD([sQuery(id+"F4.wireOp",EDGE,"E25.2.4"),sQuery(id+"F4.wireOp",EDGE,"E25.2.10")])]})});
            var Q41;
            Q41=makeQuery(id+"F5.boolean.opBoolean","COPY",EDGE,{"derivedFrom":makeQuery(id+"F5.opExtrude","SWEPT_EDGE",EDGE,{"disambiguationData":[OSD([sQuery(id+"F4.wireOp",EDGE,"E25.2.4"),sQuery(id+"F4.wireOp",EDGE,"E25.2.9")])]})});
            var Q42;
            Q42=makeQuery(id+"F5.boolean.opBoolean","COPY",EDGE,{"derivedFrom":makeQuery(id+"F5.opExtrude","SWEPT_EDGE",EDGE,{"disambiguationData":[OSD([sQuery(id+"F4.wireOp",EDGE,"E25.1.0"),sQuery(id+"F4.wireOp",EDGE,"E25.1.5")])]})});
            var Q43;
            Q43=makeQuery(id+"F7.boolean.opBoolean","INTERSECT",EDGE,{"disambiguationData":[OD(0.0)],"derivedFrom":[makeQuery(id+"F5.boolean.opBoolean","COPY",FACE,{"derivedFrom":makeQuery(id+"F5.opExtrude","SWEPT_FACE",FACE,{"disambiguationData":[OSD([sQuery(id+"F4.wireOp",EDGE,"E25.1.0"),sQuery(id+"F4.wireOp",EDGE,"E25.1.8")])]})}),makeQuery(id+"F7.opExtrude","SWEPT_FACE",FACE,{"disambiguationData":[OSD([sQuery(id+"F6.wireOp",EDGE,"E27.2.0")])]})]});
            var Q44;
            Q44=makeQuery(id+"F7.boolean.opBoolean","INTERSECT",EDGE,{"disambiguationData":[OD(1.0)],"derivedFrom":[makeQuery(id+"F5.boolean.opBoolean","COPY",FACE,{"derivedFrom":makeQuery(id+"F5.opExtrude","SWEPT_FACE",FACE,{"disambiguationData":[OSD([sQuery(id+"F4.wireOp",EDGE,"E25.1.0"),sQuery(id+"F4.wireOp",EDGE,"E25.1.8")])]})}),makeQuery(id+"F7.opExtrude","SWEPT_FACE",FACE,{"disambiguationData":[OSD([sQuery(id+"F6.wireOp",EDGE,"E27.2.0")])]})]});
            var Q45;
            Q45=makeQuery(id+"F5.boolean.opBoolean","COPY",EDGE,{"derivedFrom":makeQuery(id+"F5.opExtrude","SWEPT_EDGE",EDGE,{"disambiguationData":[OSD([sQuery(id+"F4.wireOp",EDGE,"E25.1.1"),sQuery(id+"F4.wireOp",EDGE,"E25.1.8")])]})});
            var Q46;
            Q46=makeQuery(id+"F5.boolean.opBoolean","COPY",EDGE,{"derivedFrom":makeQuery(id+"F5.opExtrude","SWEPT_EDGE",EDGE,{"disambiguationData":[OSD([sQuery(id+"F4.wireOp",EDGE,"E25.1.3"),sQuery(id+"F4.wireOp",EDGE,"E25.1.6")])]})});
            var Q47;
            Q47=makeQuery(id+"F7.boolean.opBoolean","INTERSECT",EDGE,{"derivedFrom":[makeQuery(id+"F5.boolean.opBoolean","COPY",FACE,{"derivedFrom":makeQuery(id+"F5.opExtrude","SWEPT_FACE",FACE,{"disambiguationData":[OSD([sQuery(id+"F4.wireOp",EDGE,"E25.1.3")])]})}),makeQuery(id+"F7.opExtrude","SWEPT_FACE",FACE,{"disambiguationData":[OSD([sQuery(id+"F6.wireOp",EDGE,"E27.2.0")])]})]});
            var Q48;
            Q48=makeQuery(id+"F5.boolean.opBoolean","COPY",EDGE,{"derivedFrom":makeQuery(id+"F5.opExtrude","SWEPT_EDGE",EDGE,{"disambiguationData":[OSD([sQuery(id+"F4.wireOp",EDGE,"E25.1.6"),sQuery(id+"F4.wireOp",EDGE,"E25.1.11")])]})});
            var Q49;
            Q49=makeQuery(id+"F5.boolean.opBoolean","COPY",EDGE,{"derivedFrom":makeQuery(id+"F5.opExtrude","SWEPT_EDGE",EDGE,{"disambiguationData":[OSD([sQuery(id+"F4.wireOp",EDGE,"E25.1.2"),sQuery(id+"F4.wireOp",EDGE,"E25.1.11")])]})});
            var Q50;
            Q50=makeQuery(id+"F7.boolean.opBoolean","INTERSECT",EDGE,{"derivedFrom":[makeQuery(id+"F5.boolean.opBoolean","COPY",FACE,{"derivedFrom":makeQuery(id+"F5.opExtrude","SWEPT_FACE",FACE,{"disambiguationData":[OSD([sQuery(id+"F4.wireOp",EDGE,"E25.1.2")])]})}),makeQuery(id+"F7.opExtrude","SWEPT_FACE",FACE,{"disambiguationData":[OSD([sQuery(id+"F6.wireOp",EDGE,"E27.2.0")])]})]});
            var Q51;
            Q51=makeQuery(id+"F7.boolean.opBoolean","INTERSECT",EDGE,{"derivedFrom":[makeQuery(id+"F5.boolean.opBoolean","COPY",FACE,{"derivedFrom":makeQuery(id+"F5.opExtrude","SWEPT_FACE",FACE,{"disambiguationData":[OSD([sQuery(id+"F4.wireOp",EDGE,"E25.1.7")])]})}),makeQuery(id+"F7.opExtrude","SWEPT_FACE",FACE,{"disambiguationData":[OSD([sQuery(id+"F6.wireOp",EDGE,"E27.2.0")])]})]});
            var Q52;
            Q52=makeQuery(id+"F7.boolean.opBoolean","INTERSECT",EDGE,{"derivedFrom":[makeQuery(id+"F5.boolean.opBoolean","COPY",FACE,{"derivedFrom":makeQuery(id+"F5.opExtrude","SWEPT_FACE",FACE,{"disambiguationData":[OSD([sQuery(id+"F4.wireOp",EDGE,"E25.1.9")])]})}),makeQuery(id+"F7.opExtrude","SWEPT_FACE",FACE,{"disambiguationData":[OSD([sQuery(id+"F6.wireOp",EDGE,"E27.2.0")])]})]});
            var Q53;
            Q53=makeQuery(id+"F5.boolean.opBoolean","COPY",EDGE,{"derivedFrom":makeQuery(id+"F5.opExtrude","SWEPT_EDGE",EDGE,{"disambiguationData":[OSD([sQuery(id+"F4.wireOp",EDGE,"E25.1.4"),sQuery(id+"F4.wireOp",EDGE,"E25.1.9")])]})});
            var Q54;
            Q54=makeQuery(id+"F5.boolean.opBoolean","COPY",EDGE,{"derivedFrom":makeQuery(id+"F5.opExtrude","SWEPT_EDGE",EDGE,{"disambiguationData":[OSD([sQuery(id+"F4.wireOp",EDGE,"E25.1.7"),sQuery(id+"F4.wireOp",EDGE,"E25.1.10")])]})});
            var Q55;
            Q55=makeQuery(id+"F5.boolean.opBoolean","COPY",EDGE,{"derivedFrom":makeQuery(id+"F5.opExtrude","SWEPT_EDGE",EDGE,{"disambiguationData":[OSD([sQuery(id+"F4.wireOp",EDGE,"E25.1.4"),sQuery(id+"F4.wireOp",EDGE,"E25.1.10")])]})});
            fillet(context, id + "F12", {"entities" : qUnion([Q0, Q1, Q2, Q3, Q4, Q5, Q6, Q7, Q8, Q9, Q10, Q11, Q12, Q13, Q14, Q15, Q16, Q17, Q18, Q19, Q20, Q21, Q22, Q23, Q24, Q25, Q26, Q27, Q28, Q29, Q30, Q31, Q32, Q33, Q34, Q35, Q36, Q37, Q38, Q39, Q40, Q41, Q42, Q43, Q44, Q45, Q46, Q47, Q48, Q49, Q50, Q51, Q52, Q53, Q54, Q55]), "radius" : 1 * mm, "tangentPropagation" : true, "allowEdgeOverflow" : false});
        }
    });
